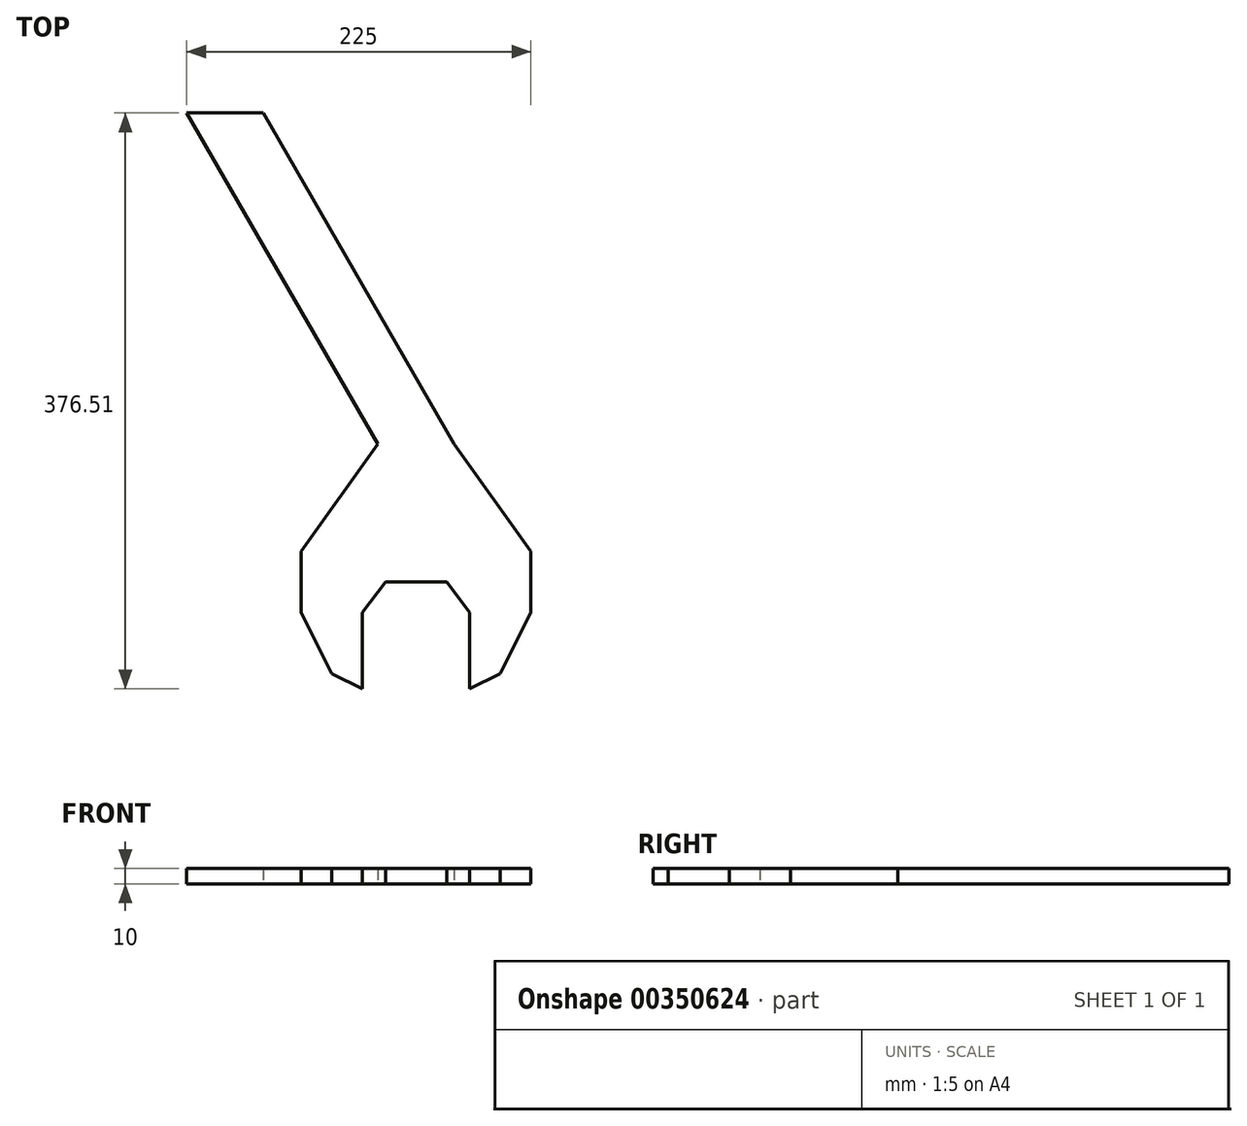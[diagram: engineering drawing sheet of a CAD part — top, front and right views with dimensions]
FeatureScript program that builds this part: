
annotation { "Feature Type Name" : "Feature", "Feature Type Description" : "" }
export const myFeature = defineFeature(function(context is Context, id is Id, definition is map)
    precondition{}
    {
        {
            var Q0;
            Q0=qCreatedBy(makeId("Top.planeOp"),FACE);
            var sketch = newSketch(context, id + "F0", { "sketchPlane" : qUnion([Q0])});
            skLineSegment(sketch, "E0", {"start": v(-20, 0) * mm, "end": v(20, 0) * mm});
            skLineSegment(sketch, "E1", {"start": v(-20, 0) * mm, "end": v(-35, -20) * mm});
            skLineSegment(sketch, "E2", {"start": v(-35, -20) * mm, "end": v(-35, -70) * mm});
            skLineSegment(sketch, "E3", {"start": v(0, 0) * mm, "end": v(0, -67.64) * mm, "construction": true});
            skLineSegment(sketch, "E4.MirrorCS", {"start": v(20, 0) * mm, "end": v(35, -20) * mm});
            skLineSegment(sketch, "E5.MirrorCS", {"start": v(35, -20) * mm, "end": v(35, -70) * mm});
            skLineSegment(sketch, "E6", {"start": v(-35, -70) * mm, "end": v(-55, -60) * mm});
            skLineSegment(sketch, "E7", {"start": v(-55, -60) * mm, "end": v(-75, -20) * mm});
            skLineSegment(sketch, "E8", {"start": v(-75, -20) * mm, "end": v(-75, 20) * mm});
            skLineSegment(sketch, "E9", {"start": v(-75, 20) * mm, "end": v(-25, 90) * mm});
            skLineSegment(sketch, "E10.MirrorCS", {"start": v(35, -70) * mm, "end": v(55, -60) * mm});
            skLineSegment(sketch, "E11.MirrorCS", {"start": v(55, -60) * mm, "end": v(75, -20) * mm});
            skLineSegment(sketch, "E12.MirrorCS", {"start": v(75, 20) * mm, "end": v(25, 90) * mm});
            skLineSegment(sketch, "E13.MirrorCS", {"start": v(75, -20) * mm, "end": v(75, 20) * mm});
            skLineSegment(sketch, "E14", {"start": v(-25, 90) * mm, "end": v(-150, 306.5) * mm});
            skLineSegment(sketch, "E15", {"start": v(-150, 306.5) * mm, "end": v(-100, 306.5) * mm});
            skLineSegment(sketch, "E16", {"start": v(-100, 306.5) * mm, "end": v(25, 90) * mm});
            skLineSegment(sketch, "E17", {"start": v(25, 90) * mm, "end": v(157.59, 90) * mm, "construction": true});
            skSolve(sketch);
        }
        {
            var Q0;
            Q0=makeQuery(id+"F0.imprint","IMPRINT",FACE,{"disambiguationData":[TD([[makeQuery(id+"F0.imprint","IMPRINT",EDGE,{"derivedFrom":sQuery(id+"F0.wireOp",EDGE,"E0")}),1.0]])]});
            extrude(context, id + "F1", {"entities" : qUnion([Q0]), "depth" : 10 * mm});
        }
    });
